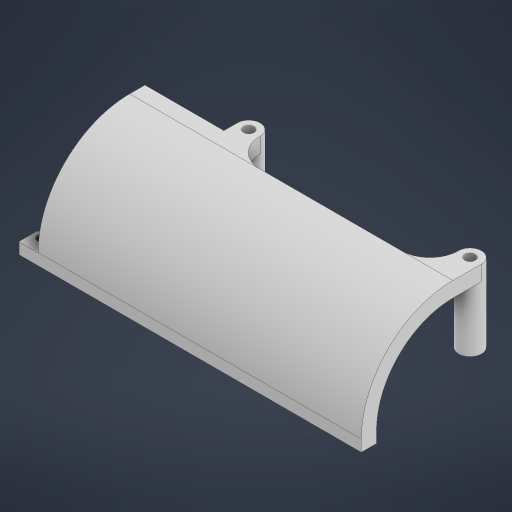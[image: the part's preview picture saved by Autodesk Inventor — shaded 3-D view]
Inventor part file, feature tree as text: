
AUTODESK INVENTOR PART (.ipt)
format: ipt  version: 2024 (Build 280153000, 153)  size: 356,864 bytes
history: native  units: mm
features: extrude x14, sketch x12, projected_geometry x8, fillet x4, chamfer x2, other x1
ambient origin geometry x8: Origin, YZ Plane, XZ Plane, XY Plane, X Axis, Y Axis, Z Axis, Center Point
bodies: Body1 (feature_tree)
feature tree (41):
  other  "솔리드1"
  extrude  "돌출1"  Depth=3.0mm
  extrude  "돌출2"  Depth=5.0mm
  extrude  "돌출3"  Depth=4.0mm
  extrude  "돌출4"  Depth=85.0mm
  sketch  "스케치5"
  extrude  "돌출5"  Depth=5.0mm
  fillet  "모깎기1"  [1 undecoded]
  fillet  "모깎기2"  Radius=3.0mm
  extrude  "돌출6"  Depth=20.0mm
  extrude  "돌출7"  Depth=80.0mm TaperAngle=0.0deg
  sketch  "스케치7"
  extrude  "돌출8"  Depth=4.7mm TaperAngle=0.0deg
  extrude  "돌출9"  Depth=6.0mm
  fillet  "모깎기4"  Radius=4.0mm
  fillet  "모깎기6"  Radius=10.5mm
  extrude  "돌출10"  Depth=2.7mm
  extrude  "돌출11"  Depth=6.0mm
  extrude  "돌출12"  Depth=16.42mm TaperAngle=0.0deg
  extrude  "돌출14"  Depth=3.0mm
  chamfer  "모따기2"  Distance=7.5mm
  chamfer  "모따기3"  Distance=16.42mm
  extrude  "돌출15"  Depth=6.0mm
  sketch  "스케치1"
  sketch  "스케치2"
  projected_geometry  "투영된 루프1"
  sketch  "스케치3"
  projected_geometry  "투영된 루프2"
  sketch  "스케치4"
  projected_geometry  "투영된 루프3"
  sketch  "스케치6"
  sketch  "스케치8"
  projected_geometry  "투영된 루프4"
  sketch  "스케치9"
  projected_geometry  "투영된 루프5"
  sketch  "스케치10"
  projected_geometry  "투영된 루프6"
  projected_geometry  "투영된 루프8"
  sketch  "스케치13"
  projected_geometry  "투영된 루프10"
  sketch  "스케치14"
note: 1 required parameter value undecoded (feature->parameter linkage not recoverable at this tier; creation-order binding heuristic only, values carry confidence <= 0.55)
